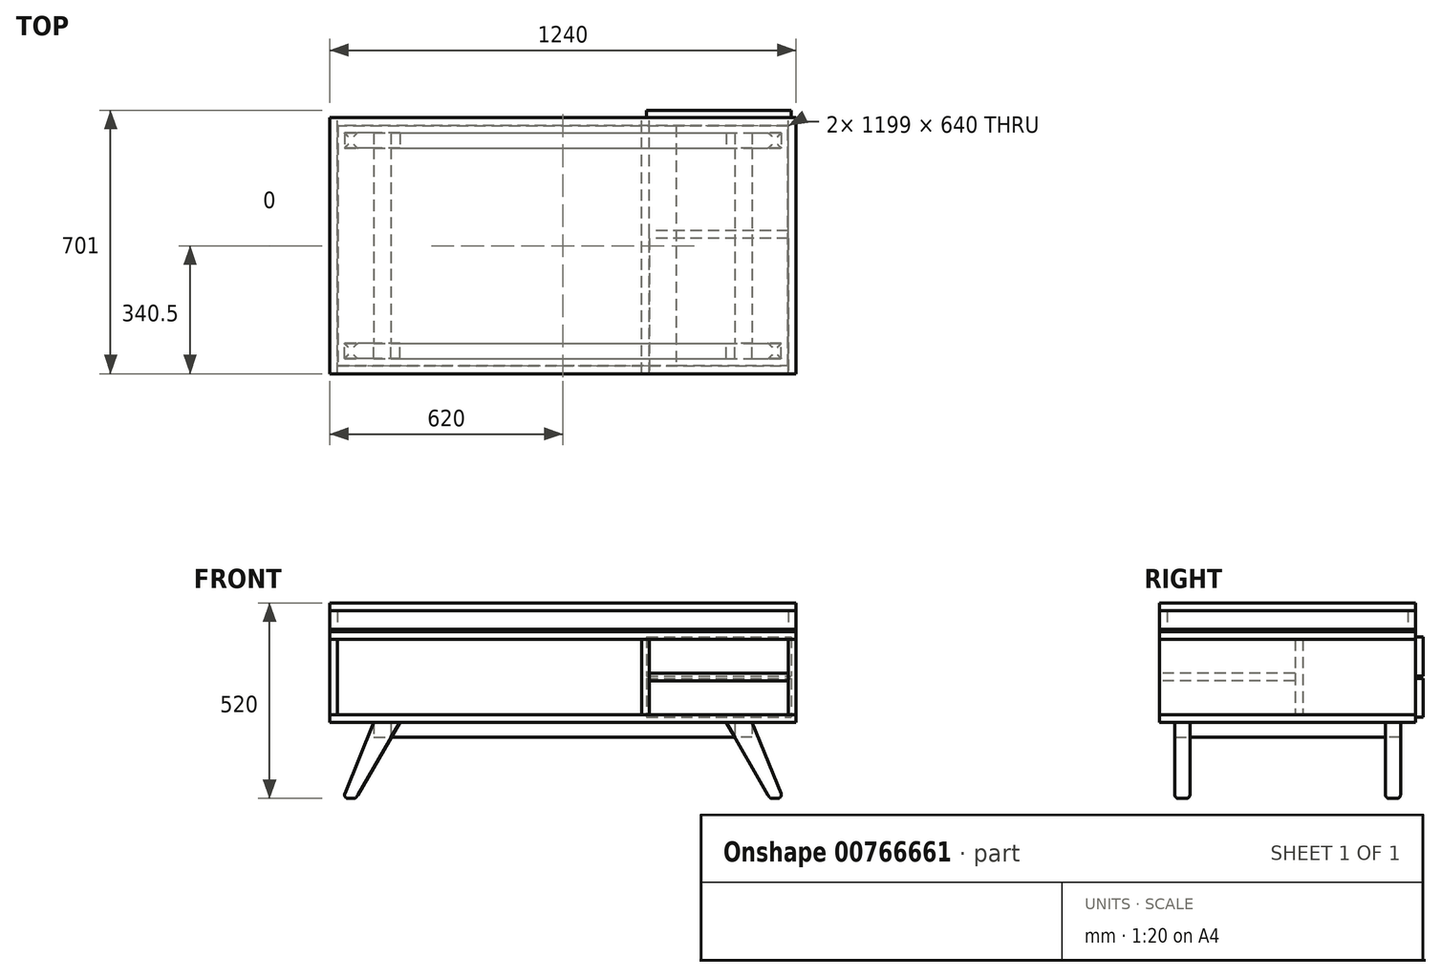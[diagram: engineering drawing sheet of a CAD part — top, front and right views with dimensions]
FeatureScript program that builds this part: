
annotation { "Feature Type Name" : "Feature", "Feature Type Description" : "" }
export const myFeature = defineFeature(function(context is Context, id is Id, definition is map)
    precondition{}
    {
        {
            var Q0;
            Q0=qCreatedBy(makeId("Front.planeOp"),FACE);
            var sketch = newSketch(context, id + "F0", { "sketchPlane" : qUnion([Q0])});
            skLineSegment(sketch, "E0.bottom", {"start": v(-620, 0) * mm, "end": v(620, 0) * mm});
            skLineSegment(sketch, "E0.top", {"start": v(-620, -241) * mm, "end": v(620, -241) * mm});
            skLineSegment(sketch, "E1", {"start": v(229.5, -20.5) * mm, "end": v(229.5, -220.5) * mm});
            skLineSegment(sketch, "E2.0", {"start": v(-620, -20.5) * mm, "end": v(620, -20.5) * mm});
            skLineSegment(sketch, "E2.2", {"start": v(-620, -220.5) * mm, "end": v(620, -220.5) * mm});
            skLineSegment(sketch, "E3.trimOffspring", {"start": v(-599.5, -20.5) * mm, "end": v(-599.5, -220.5) * mm});
            skLineSegment(sketch, "E4.trimOffspring", {"start": v(599.5, -20.5) * mm, "end": v(599.5, -220.5) * mm});
            skLineSegment(sketch, "E5.trimOffspring", {"start": v(-620, 0) * mm, "end": v(-620, -241) * mm});
            skLineSegment(sketch, "E6.trimOffspring", {"start": v(620, 0) * mm, "end": v(620, -241) * mm});
            skLineSegment(sketch, "E7", {"start": v(229.5, -120.5) * mm, "end": v(599.5, -120.5) * mm, "construction": true});
            skLineSegment(sketch, "E8", {"start": v(229.5, -110.25) * mm, "end": v(599.5, -110.25) * mm});
            skLineSegment(sketch, "E9", {"start": v(229.5, -130.75) * mm, "end": v(599.5, -130.75) * mm});
            skLineSegment(sketch, "E10.0", {"start": v(209, -20.5) * mm, "end": v(209, -220.5) * mm});
            skPoint(sketch, "E11", {"position": v(0, 0) * mm});
            skSolve(sketch);
        }
        {
            var Q0;
            {var subQ1=sQuery(id+"F0.wireOp",EDGE,"E0.top");Q0=makeQuery(id+"F0.imprint","IMPRINT",FACE,{"disambiguationData":[TD([[makeQuery(id+"F0.imprint","IMPRINT",EDGE,{"derivedFrom":subQ1}),1.0]])]});}
            extrude(context, id + "F1", {"entities" : qUnion([Q0]), "depth" : 681 / 2 * mm, "offsetDistance" : 25 * mm, "hasSecondDirection" : true, "secondDirectionOppositeDirection" : true, "secondDirectionDepth" : 681 / 2 * mm});
        }
        {
            var Q0;
            {var subQ0=sQuery(id+"F0.wireOp",EDGE,"60a11fd1-bdb7-46c1-8277-bfbef1fc92c4.0");Q0=makeQuery(id+"F0.imprint","IMPRINT",FACE,{"disambiguationData":[TD([[makeQuery(id+"F0.imprint","IMPRINT",EDGE,{"derivedFrom":subQ0}),-1.0]])]});}
            var Q1;
            {var subQ0=sQuery(id+"F0.wireOp",EDGE,"E1");Q1=makeQuery(id+"F0.imprint","IMPRINT",FACE,{"disambiguationData":[TD([[makeQuery(id+"F0.imprint","IMPRINT",EDGE,{"derivedFrom":subQ0}),-1.0]])]});}
            var Q2;
            {var subQ3=sQuery(id+"F0.wireOp",EDGE,"60a11fd1-bdb7-46c1-8277-bfbef1fc92c4.2");Q2=makeQuery(id+"F0.imprint","IMPRINT",FACE,{"disambiguationData":[TD([[makeQuery(id+"F0.imprint","IMPRINT",EDGE,{"derivedFrom":subQ3}),1.0]])]});}
            var Q3;
            {var subQ2=sQuery(id+"F0.wireOp",EDGE,"E2.2");var subQ4=sQuery(id+"F0.wireOp",EDGE,"E0.left");var subQ5=makeQuery(id+"F0.imprint","INTERSECT",VERTEX,{"derivedFrom":[subQ4,subQ2]});Q3=makeQuery(id+"F0.imprint","IMPRINT",FACE,{"disambiguationData":[TD([[makeQuery(id+"F0.imprint","IMPRINT",EDGE,{"disambiguationData":[TD([[subQ5,1.0]])],"derivedFrom":subQ4}),1.0]])]});}
            var Q4;
            {var subQ3=sQuery(id+"F0.wireOp",EDGE,"E3.trimOffspring");Q4=makeQuery(id+"F0.imprint","IMPRINT",FACE,{"disambiguationData":[TD([[makeQuery(id+"F0.imprint","IMPRINT",EDGE,{"derivedFrom":subQ3}),-1.0]])]});}
            var Q5;
            {var subQ3=sQuery(id+"F0.wireOp",EDGE,"E4.trimOffspring");Q5=makeQuery(id+"F0.imprint","IMPRINT",FACE,{"disambiguationData":[TD([[makeQuery(id+"F0.imprint","IMPRINT",EDGE,{"derivedFrom":subQ3}),1.0]])]});}
            var Q6;
            Q6=makeQuery(id+"F1.opExtrude","CAP_FACE",FACE,{"disambiguationData":[OSD([sQuery(id+"F0.wireOp",EDGE,"E0.top"),sQuery(id+"F0.wireOp",EDGE,"E0.left"),sQuery(id+"F0.wireOp",EDGE,"E0.right"),sQuery(id+"F0.wireOp",EDGE,"E2.2")])],"isStart":false});
            var Q7;
            Q7=makeQuery(id+"F1.opExtrude","CAP_FACE",FACE,{"disambiguationData":[OSD([sQuery(id+"F0.wireOp",EDGE,"E0.top"),sQuery(id+"F0.wireOp",EDGE,"E0.left"),sQuery(id+"F0.wireOp",EDGE,"E0.right"),sQuery(id+"F0.wireOp",EDGE,"E2.2")])],"isStart":true});
            extrude(context, id + "F2", {"entities" : qUnion([Q0, Q1, Q2, Q3, Q4, Q5]), "endBound" : BoundingType.UP_TO_SURFACE, "depth" : 25 * mm, "endBoundEntityFace" : qUnion([Q6]), "offsetDistance" : 25 * mm, "hasSecondDirection" : true, "secondDirectionBound" : SecondDirectionBoundingType.UP_TO_SURFACE, "secondDirectionOppositeDirection" : true, "secondDirectionDepth" : 25 * mm, "secondDirectionBoundEntityFace" : qUnion([Q7])});
        }
        {
            var Q0;
            {var subQ6=sQuery(id+"F0.wireOp",EDGE,"E0.bottom");Q0=makeQuery(id+"F0.imprint","IMPRINT",FACE,{"disambiguationData":[TD([[makeQuery(id+"F0.imprint","IMPRINT",EDGE,{"derivedFrom":subQ6}),-1.0]])]});}
            var Q1;
            Q1=makeQuery(id+"F1.opExtrude","CAP_FACE",FACE,{"disambiguationData":[OSD([sQuery(id+"F0.wireOp",EDGE,"E0.top"),sQuery(id+"F0.wireOp",EDGE,"E0.left"),sQuery(id+"F0.wireOp",EDGE,"E0.right"),sQuery(id+"F0.wireOp",EDGE,"E2.2")])],"isStart":false});
            var Q2;
            Q2=makeQuery(id+"F1.opExtrude","CAP_FACE",FACE,{"disambiguationData":[OSD([sQuery(id+"F0.wireOp",EDGE,"E0.top"),sQuery(id+"F0.wireOp",EDGE,"E0.left"),sQuery(id+"F0.wireOp",EDGE,"E0.right"),sQuery(id+"F0.wireOp",EDGE,"E2.2")])],"isStart":true});
            extrude(context, id + "F3", {"entities" : qUnion([Q0]), "endBound" : BoundingType.UP_TO_SURFACE, "depth" : 25 * mm, "endBoundEntityFace" : qUnion([Q1]), "offsetDistance" : 25 * mm, "hasSecondDirection" : true, "secondDirectionBound" : SecondDirectionBoundingType.UP_TO_SURFACE, "secondDirectionOppositeDirection" : true, "secondDirectionDepth" : 25 * mm, "secondDirectionBoundEntityFace" : qUnion([Q2])});
        }
        {
            var Q0;
            Q0=qCreatedBy(makeId("Front.planeOp"),FACE);
            cPlane(context, id + "F4", {"entities" : qUnion([Q0]), "cplaneType" : CPlaneType.OFFSET, "offset" : 260 * mm, "width" : 150 * mm, "height" : 150 * mm});
        }
        {
            var Q0;
            Q0=qCreatedBy(id+"F4.planeOp",FACE);
            var sketch = newSketch(context, id + "F5", { "sketchPlane" : qUnion([Q0])});
            skLineSegment(sketch, "E12", {"start": v(-620, -62.26) * mm, "end": v(-620, -556.12) * mm, "construction": true});
            skLineSegment(sketch, "E13", {"start": v(620, -20.15) * mm, "end": v(620, -556.12) * mm, "construction": true});
            skLineSegment(sketch, "E14", {"start": v(-1066.77, -241) * mm, "end": v(893.35, -241) * mm});
            skLineSegment(sketch, "E15", {"start": v(-503.09, -241) * mm, "end": v(-620, -443.5) * mm});
            skLineSegment(sketch, "E16", {"start": v(-620, -443.5) * mm, "end": v(-550.72, -443.5) * mm});
            skLineSegment(sketch, "E17", {"start": v(-433.8, -241) * mm, "end": v(-550.72, -443.5) * mm});
            skLineSegment(sketch, "E18.MirrorCS", {"start": v(620, -443.5) * mm, "end": v(550.72, -443.5) * mm});
            skLineSegment(sketch, "E19.MirrorCS", {"start": v(503.09, -241) * mm, "end": v(620, -443.5) * mm});
            skLineSegment(sketch, "E20.MirrorCS", {"start": v(433.8, -241) * mm, "end": v(550.72, -443.5) * mm});
            skLineSegment(sketch, "E21", {"start": v(-456.9, -281) * mm, "end": v(456.9, -281) * mm});
            skLineSegment(sketch, "E22", {"start": v(-503.09, -241) * mm, "end": v(-585.36, -443.5) * mm});
            skLineSegment(sketch, "E23", {"start": v(503.09, -241) * mm, "end": v(585.36, -443.5) * mm});
            skSolve(sketch);
        }
        {
            var Q0;
            {var subQ4=sQuery(id+"F5.wireOp",EDGE,"E22");Q0=makeQuery(id+"F5.imprint","IMPRINT",FACE,{"disambiguationData":[TD([[makeQuery(id+"F5.imprint","IMPRINT",EDGE,{"derivedFrom":subQ4}),1.0]])]});}
            var Q1;
            {var subQ4=sQuery(id+"F5.wireOp",EDGE,"E23");Q1=makeQuery(id+"F5.imprint","IMPRINT",FACE,{"disambiguationData":[TD([[makeQuery(id+"F5.imprint","IMPRINT",EDGE,{"derivedFrom":subQ4}),-1.0]])]});}
            extrude(context, id + "F6", {"entities" : qUnion([Q0, Q1]), "depth" : 40 * mm, "offsetDistance" : 25 * mm});
        }
        {
            var Q0;
            Q0=makeQuery(id+"F6.opExtrude","CAP_EDGE",EDGE,{"disambiguationData":[OSD([sQuery(id+"F5.wireOp",EDGE,"E16")])],"isStart":false});
            var Q1;
            Q1=makeQuery(id+"F6.opExtrude","SWEPT_EDGE",EDGE,{"disambiguationData":[OSD([sQuery(id+"F5.wireOp",EDGE,"E16"),sQuery(id+"F5.wireOp",EDGE,"E17")])]});
            var Q2;
            Q2=makeQuery(id+"F6.opExtrude","CAP_EDGE",EDGE,{"disambiguationData":[OSD([sQuery(id+"F5.wireOp",EDGE,"E16")])],"isStart":true});
            var Q3;
            Q3=makeQuery(id+"F6.opExtrude","SWEPT_EDGE",EDGE,{"disambiguationData":[OSD([sQuery(id+"F5.wireOp",EDGE,"E15"),sQuery(id+"F5.wireOp",EDGE,"E16")])]});
            var Q4;
            Q4=makeQuery(id+"F6.opExtrude","CAP_EDGE",EDGE,{"disambiguationData":[OSD([sQuery(id+"F5.wireOp",EDGE,"E18.MirrorCS")])],"isStart":false});
            var Q5;
            Q5=makeQuery(id+"F6.opExtrude","SWEPT_EDGE",EDGE,{"disambiguationData":[OSD([sQuery(id+"F5.wireOp",EDGE,"E18.MirrorCS"),sQuery(id+"F5.wireOp",EDGE,"E20.MirrorCS")])]});
            var Q6;
            Q6=makeQuery(id+"F6.opExtrude","CAP_EDGE",EDGE,{"disambiguationData":[OSD([sQuery(id+"F5.wireOp",EDGE,"E18.MirrorCS")])],"isStart":true});
            var Q7;
            Q7=makeQuery(id+"F6.opExtrude","SWEPT_EDGE",EDGE,{"disambiguationData":[OSD([sQuery(id+"F5.wireOp",EDGE,"E18.MirrorCS"),sQuery(id+"F5.wireOp",EDGE,"E19.MirrorCS")])]});
            fillet(context, id + "F7", {"entities" : qUnion([Q0, Q1, Q2, Q3, Q4, Q5, Q6, Q7]), "tangentPropagation" : true, "radius" : 10 * mm, "defaultsChanged" : true, "vertexSettings" : [], "allowEdgeOverflow" : false});
        }
        {
            var Q0;
            {var subQ5=sQuery(id+"F5.wireOp",EDGE,"E21");Q0=makeQuery(id+"F5.imprint","IMPRINT",FACE,{"disambiguationData":[TD([[makeQuery(id+"F5.imprint","IMPRINT",EDGE,{"derivedFrom":subQ5}),1.0]])]});}
            extrude(context, id + "F8", {"entities" : qUnion([Q0]), "depth" : 40 * mm, "offsetDistance" : 25 * mm});
        }
        {
            var Q0;
            Q0=makeQuery(id+"F6.opExtrude","SWEPT_BODY",BODY,{"disambiguationData":[OSD([sQuery(id+"F5.wireOp",EDGE,"E14"),sQuery(id+"F5.wireOp",EDGE,"E15"),sQuery(id+"F5.wireOp",EDGE,"E16"),sQuery(id+"F5.wireOp",EDGE,"E17")])]});
            var Q1;
            Q1=makeQuery(id+"F6.opExtrude","SWEPT_BODY",BODY,{"disambiguationData":[OSD([sQuery(id+"F5.wireOp",EDGE,"E14"),sQuery(id+"F5.wireOp",EDGE,"E18.MirrorCS"),sQuery(id+"F5.wireOp",EDGE,"E19.MirrorCS"),sQuery(id+"F5.wireOp",EDGE,"E20.MirrorCS")])]});
            var Q2;
            Q2=makeQuery(id+"F8.opExtrude","SWEPT_BODY",BODY,{"disambiguationData":[OSD([sQuery(id+"F5.wireOp",EDGE,"E14"),sQuery(id+"F5.wireOp",EDGE,"E17"),sQuery(id+"F5.wireOp",EDGE,"E20.MirrorCS"),sQuery(id+"F5.wireOp",EDGE,"E21")])]});
            var Q3;
            Q3=qCreatedBy(makeId("Front.planeOp"),FACE);
            mirror(context, id + "F9", {"entities" : qUnion([Q0, Q1, Q2]), "mirrorPlane" : qUnion([Q3])});
        }
        {
            var Q0;
            {var subQ5=sQuery(id+"F5.wireOp",EDGE,"E18.MirrorCS");Q0=makeQuery(id+"F5.imprint","IMPRINT",FACE,{"disambiguationData":[TD([[makeQuery(id+"F5.imprint","IMPRINT",EDGE,{"derivedFrom":subQ5}),-1.0]])]});}
            var sketch = newSketch(context, id + "F10", { "sketchPlane" : qUnion([Q0])});
            skPoint(sketch, "E24.0", {"position": v(503.09, -241) * mm});
            skPoint(sketch, "E25.0", {"position": v(456.9, -281) * mm});
            skLineSegment(sketch, "E26.bottom", {"start": v(503.09, -241) * mm, "end": v(456.9, -241) * mm});
            skLineSegment(sketch, "E26.top", {"start": v(503.09, -281) * mm, "end": v(456.9, -281) * mm});
            skLineSegment(sketch, "E26.left", {"start": v(503.09, -241) * mm, "end": v(503.09, -281) * mm});
            skLineSegment(sketch, "E26.right", {"start": v(456.9, -241) * mm, "end": v(456.9, -281) * mm});
            skLineSegment(sketch, "E27.MirrorCS", {"start": v(-503.09, -241) * mm, "end": v(-456.9, -241) * mm});
            skLineSegment(sketch, "E28.MirrorCS", {"start": v(-456.9, -241) * mm, "end": v(-456.9, -281) * mm});
            skLineSegment(sketch, "E29.MirrorCS", {"start": v(-503.09, -241) * mm, "end": v(-503.09, -281) * mm});
            skLineSegment(sketch, "E30.MirrorCS", {"start": v(-503.09, -281) * mm, "end": v(-456.9, -281) * mm});
            skSolve(sketch);
        }
        {
            var Q0;
            Q0=qSketchRegion(id+"F10",true);
            extrude(context, id + "F11", {"entities" : qUnion([Q0]), "endBound" : BoundingType.UP_TO_NEXT, "oppositeDirection" : true, "depth" : 25 * mm, "offsetDistance" : 25 * mm});
        }
        {
            var Q0;
            Q0=makeQuery(id+"F2.opExtrude","CAP_FACE",FACE,{"disambiguationData":[OSD([sQuery(id+"F0.wireOp",EDGE,"E1"),sQuery(id+"F0.wireOp",EDGE,"E2.0"),sQuery(id+"F0.wireOp",EDGE,"E2.2"),sQuery(id+"F0.wireOp",EDGE,"ae8f2980-7300-4422-b546-210f4e41f4ac.trimOffspring"),sQuery(id+"F0.wireOp",EDGE,"E4.trimOffspring"),sQuery(id+"F0.wireOp",EDGE,"E6.trimOffspring"),sQuery(id+"F0.wireOp",EDGE,"E8"),sQuery(id+"F0.wireOp",EDGE,"E9")])],"isStart":true});
            var sketch = newSketch(context, id + "F12", { "sketchPlane" : qUnion([Q0])});
            skPoint(sketch, "E31.orphan", {"position": v(620, -20.5) * mm});
            skPoint(sketch, "E32.orphan", {"position": v(620, -220.5) * mm});
            skLineSegment(sketch, "E33.0", {"start": v(-229.5, -20.5) * mm, "end": v(-599.5, -20.5) * mm, "construction": true});
            skLineSegment(sketch, "E34.0", {"start": v(-599.5, -20.5) * mm, "end": v(-599.5, -110.25) * mm, "construction": true});
            skLineSegment(sketch, "E35.0", {"start": v(-229.5, -220.5) * mm, "end": v(-599.5, -220.5) * mm, "construction": true});
            skLineSegment(sketch, "E36.0", {"start": v(-229.5, -20.5) * mm, "end": v(-229.5, -110.25) * mm, "construction": true});
            skLineSegment(sketch, "E37.0", {"start": v(-229.5, -110.25) * mm, "end": v(-599.5, -110.25) * mm, "construction": true});
            skLineSegment(sketch, "E38.0", {"start": v(-229.5, -130.75) * mm, "end": v(-599.5, -130.75) * mm, "construction": true});
            skLineSegment(sketch, "E39.trimOffspring", {"start": v(-599.5, -130.75) * mm, "end": v(-599.5, -220.5) * mm, "construction": true});
            skLineSegment(sketch, "E40.trimOffspring", {"start": v(-229.5, -130.75) * mm, "end": v(-229.5, -220.5) * mm, "construction": true});
            skPoint(sketch, "E41.orphan", {"position": v(-620, -220.5) * mm});
            skPoint(sketch, "E42.orphan", {"position": v(-620, -20.5) * mm});
            skLineSegment(sketch, "E43.0", {"start": v(-222.5, -13.5) * mm, "end": v(-606.5, -13.5) * mm});
            skLineSegment(sketch, "E43.1", {"start": v(-222.5, -13.5) * mm, "end": v(-222.5, -117.25) * mm});
            skLineSegment(sketch, "E43.2", {"start": v(-222.5, -117.25) * mm, "end": v(-606.5, -117.25) * mm});
            skLineSegment(sketch, "E43.3", {"start": v(-606.5, -13.5) * mm, "end": v(-606.5, -117.25) * mm});
            skLineSegment(sketch, "E44.0", {"start": v(-222.5, -123.75) * mm, "end": v(-606.5, -123.75) * mm});
            skLineSegment(sketch, "E44.1", {"start": v(-222.5, -123.75) * mm, "end": v(-222.5, -227.5) * mm});
            skLineSegment(sketch, "E44.2", {"start": v(-222.5, -227.5) * mm, "end": v(-606.5, -227.5) * mm});
            skLineSegment(sketch, "E44.3", {"start": v(-606.5, -123.75) * mm, "end": v(-606.5, -227.5) * mm});
            skSolve(sketch);
        }
        {
            var Q0;
            {var subQ0=sQuery(id+"F12.wireOp",EDGE,"E43.3");var subQ1=sQuery(id+"F12.wireOp",EDGE,"E43.2");var subQ2=makeQuery(id+"F12.imprint","INTERSECT",VERTEX,{"derivedFrom":[subQ1,subQ0]});Q0=makeQuery(id+"F12.imprint","IMPRINT",FACE,{"disambiguationData":[TD([[makeQuery(id+"F12.imprint","IMPRINT",EDGE,{"disambiguationData":[TD([[subQ2,1.0]])],"derivedFrom":subQ1}),-1.0]])]});}
            var Q1;
            {var subQ1=sQuery(id+"F12.wireOp",EDGE,"E43.0");Q1=makeQuery(id+"F12.imprint","IMPRINT",FACE,{"disambiguationData":[TD([[makeQuery(id+"F12.imprint","IMPRINT",EDGE,{"derivedFrom":subQ1}),1.0]])]});}
            var Q2;
            {var subQ0=sQuery(id+"F12.wireOp",EDGE,"E44.3");var subQ1=sQuery(id+"F12.wireOp",EDGE,"E44.0");var subQ2=makeQuery(id+"F12.imprint","INTERSECT",VERTEX,{"derivedFrom":[subQ1,subQ0]});Q2=makeQuery(id+"F12.imprint","IMPRINT",FACE,{"disambiguationData":[TD([[makeQuery(id+"F12.imprint","IMPRINT",EDGE,{"disambiguationData":[TD([[subQ2,1.0]])],"derivedFrom":subQ1}),1.0]])]});}
            var Q3;
            {var subQ1=sQuery(id+"F12.wireOp",EDGE,"E44.1");Q3=makeQuery(id+"F12.imprint","IMPRINT",FACE,{"disambiguationData":[TD([[makeQuery(id+"F12.imprint","IMPRINT",EDGE,{"derivedFrom":subQ1}),-1.0]])]});}
            extrude(context, id + "F13", {"entities" : qUnion([Q0, Q1, Q2, Q3]), "depth" : 20 * mm, "offsetDistance" : 25 * mm});
        }
        {
            var Q0;
            Q0=makeQuery(id+"F3.opExtrude","SWEPT_FACE",FACE,{"disambiguationData":[OSD([sQuery(id+"F0.wireOp",EDGE,"E0.bottom")])]});
            var sketch = newSketch(context, id + "F14", { "sketchPlane" : qUnion([Q0])});
            skLineSegment(sketch, "E45.0", {"start": v(-620, -340.5) * mm, "end": v(-620, 340.5) * mm});
            skLineSegment(sketch, "E45.1", {"start": v(-620, 340.5) * mm, "end": v(620, 340.5) * mm});
            skLineSegment(sketch, "E45.2", {"start": v(620, -340.5) * mm, "end": v(620, 340.5) * mm});
            skLineSegment(sketch, "E45.3", {"start": v(-620, -340.5) * mm, "end": v(620, -340.5) * mm});
            skLineSegment(sketch, "E46.0", {"start": v(-599.5, 320) * mm, "end": v(-599.5, -320) * mm});
            skLineSegment(sketch, "E46.1", {"start": v(599.5, 320) * mm, "end": v(-599.5, 320) * mm});
            skLineSegment(sketch, "E46.2", {"start": v(599.5, -320) * mm, "end": v(599.5, 320) * mm});
            skLineSegment(sketch, "E46.3", {"start": v(-599.5, -320) * mm, "end": v(599.5, -320) * mm});
            skLineSegment(sketch, "E47.0", {"start": v(-615, 335.5) * mm, "end": v(-615, -335.5) * mm});
            skLineSegment(sketch, "E47.1", {"start": v(615, 335.5) * mm, "end": v(-615, 335.5) * mm});
            skLineSegment(sketch, "E47.2", {"start": v(615, -335.5) * mm, "end": v(615, 335.5) * mm});
            skLineSegment(sketch, "E47.3", {"start": v(-615, -335.5) * mm, "end": v(615, -335.5) * mm});
            skSolve(sketch);
        }
        {
            var Q0;
            Q0=makeQuery(id+"F14.imprint","IMPRINT",FACE,{"disambiguationData":[TD([[makeQuery(id+"F14.imprint","IMPRINT",EDGE,{"derivedFrom":sQuery(id+"F14.wireOp",EDGE,"E46.0")}),-1.0]])]});
            var Q1;
            Q1=makeQuery(id+"F14.imprint","IMPRINT",FACE,{"disambiguationData":[TD([[makeQuery(id+"F14.imprint","IMPRINT",EDGE,{"derivedFrom":sQuery(id+"F14.wireOp",EDGE,"E45.0")}),-1.0]])]});
            extrude(context, id + "F15", {"entities" : qUnion([Q0, Q1]), "depth" : 6 * mm, "offsetDistance" : 25 * mm});
        }
        {
            var Q0;
            Q0=makeQuery(id+"F3.opExtrude","SWEPT_FACE",FACE,{"disambiguationData":[OSD([sQuery(id+"F0.wireOp",EDGE,"E0.bottom")])]});
            var sketch = newSketch(context, id + "F16", { "sketchPlane" : qUnion([Q0])});
            skLineSegment(sketch, "E48.0", {"start": v(599.5, 320) * mm, "end": v(-599.5, 320) * mm});
            skLineSegment(sketch, "E48.1", {"start": v(-599.5, 320) * mm, "end": v(-599.5, -320) * mm});
            skLineSegment(sketch, "E48.2", {"start": v(-599.5, -320) * mm, "end": v(599.5, -320) * mm});
            skLineSegment(sketch, "E48.3", {"start": v(599.5, -320) * mm, "end": v(599.5, 320) * mm});
            skLineSegment(sketch, "E49", {"start": v(300.5, 320) * mm, "end": v(300.5, -320) * mm});
            skLineSegment(sketch, "E50.0", {"start": v(598, 318.5) * mm, "end": v(-598, 318.5) * mm});
            skLineSegment(sketch, "E50.1", {"start": v(598, -318.5) * mm, "end": v(598, 318.5) * mm});
            skLineSegment(sketch, "E50.2", {"start": v(-598, -318.5) * mm, "end": v(598, -318.5) * mm});
            skLineSegment(sketch, "E50.3", {"start": v(-598, 318.5) * mm, "end": v(-598, -318.5) * mm});
            skSolve(sketch);
        }
        {
            var Q0;
            {var subQ5=sQuery(id+"F16.wireOp",EDGE,"E50.3");Q0=makeQuery(id+"F16.imprint","IMPRINT",FACE,{"disambiguationData":[TD([[makeQuery(id+"F16.imprint","IMPRINT",EDGE,{"derivedFrom":subQ5}),1.0]])]});}
            extrude(context, id + "F17", {"entities" : qUnion([Q0]), "depth" : 3 * mm, "offsetDistance" : 25 * mm});
        }
        {
            var Q0;
            {var subQ5=sQuery(id+"F16.wireOp",EDGE,"E50.1");Q0=makeQuery(id+"F16.imprint","IMPRINT",FACE,{"disambiguationData":[TD([[makeQuery(id+"F16.imprint","IMPRINT",EDGE,{"derivedFrom":subQ5}),1.0]])]});}
            var Q1;
            Q1=makeQuery(id+"F17.opExtrude","CAP_FACE",FACE,{"disambiguationData":[OSD([sQuery(id+"F16.wireOp",EDGE,"E48.0"),sQuery(id+"F16.wireOp",EDGE,"E48.1"),sQuery(id+"F16.wireOp",EDGE,"E48.2"),sQuery(id+"F16.wireOp",EDGE,"E49")])],"isStart":false});
            extrude(context, id + "F18", {"entities" : qUnion([Q0]), "endBound" : BoundingType.UP_TO_SURFACE, "depth" : 25 * mm, "endBoundEntityFace" : qUnion([Q1]), "offsetDistance" : 25 * mm});
        }
        {
            var Q0;
            Q0=makeQuery(id+"F15.opExtrude","CAP_FACE",FACE,{"disambiguationData":[OSD([sQuery(id+"F14.wireOp",EDGE,"E45.0"),sQuery(id+"F14.wireOp",EDGE,"E45.1"),sQuery(id+"F14.wireOp",EDGE,"E45.2"),sQuery(id+"F14.wireOp",EDGE,"E45.3"),sQuery(id+"F14.wireOp",EDGE,"E46.0"),sQuery(id+"F14.wireOp",EDGE,"E46.1"),sQuery(id+"F14.wireOp",EDGE,"E46.2"),sQuery(id+"F14.wireOp",EDGE,"E46.3")])],"isStart":false});
            extrude(context, id + "F19", {"entities" : qUnion([Q0]), "depth" : 50 * mm, "offsetDistance" : 25 * mm});
        }
        {
            var Q0;
            Q0=makeQuery(id+"F19.opExtrude","CAP_FACE",FACE,{"disambiguationData":[OSD([sQuery(id+"F14.wireOp",EDGE,"E45.0"),sQuery(id+"F14.wireOp",EDGE,"E45.1"),sQuery(id+"F14.wireOp",EDGE,"E45.2"),sQuery(id+"F14.wireOp",EDGE,"E45.3"),sQuery(id+"F14.wireOp",EDGE,"E46.0"),sQuery(id+"F14.wireOp",EDGE,"E46.1"),sQuery(id+"F14.wireOp",EDGE,"E46.2"),sQuery(id+"F14.wireOp",EDGE,"E46.3")])],"isStart":false});
            var sketch = newSketch(context, id + "F20", { "sketchPlane" : qUnion([Q0])});
            skLineSegment(sketch, "E51.0", {"start": v(-620, 340.5) * mm, "end": v(620, 340.5) * mm});
            skLineSegment(sketch, "E52.0", {"start": v(-620, -340.5) * mm, "end": v(-620, 340.5) * mm});
            skLineSegment(sketch, "E53.0", {"start": v(-620, -340.5) * mm, "end": v(620, -340.5) * mm});
            skLineSegment(sketch, "E54.0", {"start": v(620, -340.5) * mm, "end": v(620, 340.5) * mm});
            skSolve(sketch);
        }
        {
            var Q0;
            Q0=qSketchRegion(id+"F20",true);
            extrude(context, id + "F21", {"entities" : qUnion([Q0]), "depth" : 20.5 * mm, "offsetDistance" : 25 * mm});
        }
        {
            var Q0;
            Q0=makeQuery(id+"F2.opExtrude","SWEPT_FACE",FACE,{"disambiguationData":[OSD([sQuery(id+"F0.wireOp",EDGE,"E1")])]});
            var sketch = newSketch(context, id + "F22", { "sketchPlane" : qUnion([Q0])});
            skLineSegment(sketch, "E55.0", {"start": v(-340.5, -20.5) * mm, "end": v(-340.5, -220.5) * mm, "construction": true});
            skLineSegment(sketch, "E56.0", {"start": v(340.5, -20.5) * mm, "end": v(340.5, -220.5) * mm, "construction": true});
            skLineSegment(sketch, "E57.2", {"start": v(19.5, -20.5) * mm, "end": v(40, -20.5) * mm});
            skLineSegment(sketch, "E57.3", {"start": v(19.5, -220.5) * mm, "end": v(40, -220.5) * mm});
            skLineSegment(sketch, "E58", {"start": v(19.5, -20.5) * mm, "end": v(19.5, -130.75) * mm});
            skLineSegment(sketch, "E59", {"start": v(40, -20.5) * mm, "end": v(40, -130.75) * mm});
            skLineSegment(sketch, "E60", {"start": v(40, -220.5) * mm, "end": v(19.5, -220.5) * mm});
            skPoint(sketch, "E61.orphan", {"position": v(-340.5, -220.5) * mm});
            skPoint(sketch, "E62.orphan", {"position": v(340.5, -220.5) * mm});
            skPoint(sketch, "E63.orphan", {"position": v(340.5, -110.25) * mm});
            skPoint(sketch, "E64.orphan", {"position": v(340.5, -130.75) * mm});
            skPoint(sketch, "E65.orphan", {"position": v(-340.5, -110.25) * mm});
            skPoint(sketch, "E66.orphan", {"position": v(-340.5, -130.75) * mm});
            skLineSegment(sketch, "E67.trimOffspring", {"start": v(40, -130.75) * mm, "end": v(40, -220.5) * mm});
            skLineSegment(sketch, "E68.trimOffspring", {"start": v(19.5, -130.75) * mm, "end": v(19.5, -220.5) * mm});
            skSolve(sketch);
        }
        {
            var Q0;
            Q0=makeQuery(id+"F22.imprint","IMPRINT",FACE,{"disambiguationData":[TD([[makeQuery(id+"F22.imprint","IMPRINT",EDGE,{"derivedFrom":sQuery(id+"F22.wireOp",EDGE,"E58")}),1.0]])]});
            extrude(context, id + "F23", {"entities" : qUnion([Q0]), "endBound" : BoundingType.UP_TO_NEXT, "depth" : 25 * mm, "offsetDistance" : 25 * mm});
        }
        {
            var Q0;
            {var subQ2=sQuery(id+"F0.wireOp",EDGE,"E8");Q0=makeQuery(id+"F0.imprint","IMPRINT",FACE,{"disambiguationData":[TD([[makeQuery(id+"F0.imprint","IMPRINT",EDGE,{"derivedFrom":subQ2}),-1.0]])]});}
            var Q1;
            Q1=makeQuery(id+"F2.opExtrude","CAP_FACE",FACE,{"disambiguationData":[OSD([sQuery(id+"F0.wireOp",EDGE,"E1"),sQuery(id+"F0.wireOp",EDGE,"E2.0"),sQuery(id+"F0.wireOp",EDGE,"E2.2"),sQuery(id+"F0.wireOp",EDGE,"E10.0")])],"isStart":false});
            extrude(context, id + "F24", {"entities" : qUnion([Q0]), "endBound" : BoundingType.UP_TO_NEXT, "oppositeDirection" : true, "depth" : 25 * mm, "offsetDistance" : 25 * mm, "hasSecondDirection" : true, "secondDirectionBound" : SecondDirectionBoundingType.UP_TO_SURFACE, "secondDirectionOppositeDirection" : false, "secondDirectionDepth" : 25 * mm, "secondDirectionBoundEntityFace" : qUnion([Q1])});
        }
    });
